FCSTD DOCUMENT  (FreeCAD 0.19R24276 (Git))
Label: Paper_knife
License: All rights reserved
LicenseURL: http://en.wikipedia.org/wiki/All_rights_reserved
objects: Sketcher::SketchObject×2, PartDesign::Body×1
note: 3 computed .brp shape members not serialized (recipe doc carries the construction recipe); baked Part::Feature solids carry a one-line shape summary decoded from their .brp

FEATURE [Sketcher::SketchObject] Sketch  label="Sketch_paper_knife"
  FullyConstrained = false
  MapMode = 5
  Support = -> [XY_Plane]
  sketch-geometry (54):
    g0: Circle CenterX=0 CenterY=0 CenterZ=0 NormalX=0 NormalY=0 NormalZ=1 AngleXU=0 Radius=70
    g1: LineSegment StartX=0 StartY=0 StartZ=0 EndX=-30.5434 EndY=62.9849 EndZ=0
    g2: Circle CenterX=200 CenterY=0 CenterZ=0 NormalX=0 NormalY=0 NormalZ=1 AngleXU=0 Radius=70
    g3: LineSegment StartX=200 StartY=0 StartZ=0 EndX=169.457 EndY=62.9849 EndZ=0
    g4: LineSegment StartX=169.457 StartY=62.9849 StartZ=0 EndX=-30.5434 EndY=62.9849 EndZ=0
    g5: LineSegment StartX=-234.473 StartY=320.288 StartZ=0 EndX=-134.473 EndY=320.288 EndZ=0
    g6: LineSegment StartX=-224.473 StartY=338.288 StartZ=0 EndX=-124.473 EndY=338.288 EndZ=0
    g7: LineSegment StartX=-134.473 StartY=320.288 StartZ=0 EndX=-124.473 EndY=338.288 EndZ=0
    g8: LineSegment StartX=-234.473 StartY=320.288 StartZ=0 EndX=-224.473 EndY=338.288 EndZ=0
    g9: Circle CenterX=-140.473 CenterY=329.288 CenterZ=0 NormalX=0 NormalY=0 NormalZ=1 AngleXU=0 Radius=2.3784
    g10: LineSegment StartX=-233.473 StartY=322.088 StartZ=0 EndX=-133.473 EndY=322.088 EndZ=0
    g11: Circle CenterX=0 CenterY=0 CenterZ=0 NormalX=0 NormalY=0 NormalZ=1 AngleXU=0 Radius=37.5
    g12: Circle CenterX=200 CenterY=0 CenterZ=0 NormalX=0 NormalY=0 NormalZ=1 AngleXU=0 Radius=37.5
    g13: Circle CenterX=169.457 CenterY=62.9849 CenterZ=0 NormalX=0 NormalY=0 NormalZ=1 AngleXU=0 Radius=8
    g14: Circle CenterX=-30.5434 CenterY=62.9849 CenterZ=0 NormalX=0 NormalY=0 NormalZ=1 AngleXU=0 Radius=8
    g15: Circle CenterX=169.457 CenterY=62.9849 CenterZ=0 NormalX=0 NormalY=0 NormalZ=1 AngleXU=0 Radius=2.5
    g16: Circle CenterX=-30.5434 CenterY=62.9849 CenterZ=0 NormalX=0 NormalY=0 NormalZ=1 AngleXU=0 Radius=2.5
    g17: Circle CenterX=70.5033 CenterY=148.864 CenterZ=0 NormalX=0 NormalY=0 NormalZ=1 AngleXU=0 Radius=2.5
    g18: LineSegment StartX=-51.9967 StartY=177.072 StartZ=0 EndX=70.5033 EndY=177.072 EndZ=0
    g19: ArcOfCircle CenterX=75.3046 CenterY=153.864 CenterZ=0 NormalX=0 NormalY=0 NormalZ=1 AngleXU=0 Radius=16 StartAngle=4.17347 EndAngle=5.96536
    g20: LineSegment StartX=75.3046 StartY=153.864 StartZ=0 EndX=75.3046 EndY=137.864 EndZ=0
    g21: ArcOfCircle CenterX=-27.4967 CenterY=156.388 CenterZ=0 NormalX=0 NormalY=0 NormalZ=1 AngleXU=0 Radius=8 StartAngle=3.71141 EndAngle=5.43055
    g22: LineSegment StartX=-59.4967 StartY=163.072 StartZ=0 EndX=-51.9967 EndY=177.072 EndZ=0
    g23: LineSegment StartX=-59.4967 StartY=163.072 StartZ=0 EndX=-55.4967 EndY=152.072 EndZ=0
    g24: ArcOfCircle CenterX=30.0139 CenterY=78.0754 CenterZ=0 NormalX=0 NormalY=0 NormalZ=1 AngleXU=0 Radius=72.29 StartAngle=1.03221 EndAngle=1.56403
    g25: LineSegment StartX=30.5033 StartY=150.364 StartZ=0 EndX=-22.2327 EndY=150.364 EndZ=0
    g26: LineSegment StartX=-34.2327 StartY=152.072 StartZ=0 EndX=-55.4967 EndY=152.072 EndZ=0
    g27: ArcOfCircle CenterX=64.5033 CenterY=151.624 CenterZ=0 NormalX=0 NormalY=0 NormalZ=1 AngleXU=0 Radius=26.1461 StartAngle=6.17743 EndAngle=7.62244
    g28: LineSegment StartX=70.5033 StartY=148.864 StartZ=0 EndX=90.5033 EndY=148.864 EndZ=0
    g29: ArcOfCircle CenterX=-48.4967 CenterY=163.072 CenterZ=0 NormalX=0 NormalY=0 NormalZ=1 AngleXU=0 Radius=2.5 StartAngle=1.5708 EndAngle=4.71239
    g30: ArcOfCircle CenterX=41.5033 CenterY=163.072 CenterZ=0 NormalX=0 NormalY=0 NormalZ=1 AngleXU=0 Radius=2.5 StartAngle=4.71239 EndAngle=7.85398
    g31: LineSegment StartX=-48.4967 StartY=160.572 StartZ=0 EndX=41.5033 EndY=160.572 EndZ=0
    g32: LineSegment StartX=-48.4967 StartY=165.572 StartZ=0 EndX=41.5033 EndY=165.572 EndZ=0
    g33: LineSegment StartX=-27.3628 StartY=293.719 StartZ=0 EndX=-27.3628 EndY=353.575 EndZ=0
    g34: LineSegment StartX=-142.497 StartY=154.072 StartZ=0 EndX=-42.4967 EndY=154.072 EndZ=0
    g35: LineSegment StartX=-132.497 StartY=172.072 StartZ=0 EndX=-32.4967 EndY=172.072 EndZ=0
    g36: LineSegment StartX=-42.4967 StartY=154.072 StartZ=0 EndX=-32.4967 EndY=172.072 EndZ=0
    g37: LineSegment StartX=-142.497 StartY=154.072 StartZ=0 EndX=-132.497 EndY=172.072 EndZ=0
    g38: Circle CenterX=-48.4967 CenterY=163.072 CenterZ=0 NormalX=0 NormalY=0 NormalZ=1 AngleXU=0 Radius=2.3784
    g39: LineSegment StartX=-141.497 StartY=155.872 StartZ=0 EndX=-41.4967 EndY=155.872 EndZ=0
    g40: LineSegment StartX=-69.9968 StartY=0.665106 StartZ=0 EndX=-139.997 EndY=0.665106 EndZ=0
    g41: Circle CenterX=-89.4605 CenterY=142.072 CenterZ=0 NormalX=0 NormalY=0 NormalZ=1 AngleXU=0 Radius=8
    g42: Circle CenterX=60.5395 CenterY=142.072 CenterZ=0 NormalX=0 NormalY=0 NormalZ=1 AngleXU=0 Radius=8
    g43: LineSegment StartX=60.5395 StartY=142.072 StartZ=0 EndX=-89.4605 EndY=142.072 EndZ=0
    g44: LineSegment StartX=-57.421 StartY=157.364 StartZ=0 EndX=70.5033 EndY=157.364 EndZ=0
    g45: LineSegment StartX=-57.7333 StartY=166.364 StartZ=0 EndX=57.5033 EndY=166.364 EndZ=0
    g46: LineSegment StartX=73.0033 StartY=148.864 StartZ=0 EndX=73.0033 EndY=154.864 EndZ=0
    g47: LineSegment StartX=70.5033 StartY=148.864 StartZ=0 EndX=73.0033 EndY=148.864 EndZ=0
    g48: ArcOfCircle CenterX=70.5033 CenterY=154.864 CenterZ=0 NormalX=0 NormalY=0 NormalZ=1 AngleXU=0 Radius=2.5 StartAngle=-9e-16 EndAngle=1.5708
    g49: LineSegment StartX=73.0033 StartY=154.864 StartZ=0 EndX=70.5033 EndY=154.864 EndZ=0
    g50: LineSegment StartX=70.5033 StartY=148.864 StartZ=0 EndX=70.5033 EndY=157.364 EndZ=0
    g51: LineSegment StartX=70.5033 StartY=148.864 StartZ=0 EndX=70.5033 EndY=177.072 EndZ=0
    g52: LineSegment StartX=64.0033 StartY=172.864 StartZ=0 EndX=64.0033 EndY=177.072 EndZ=0
    g53: LineSegment StartX=57.5033 StartY=166.364 StartZ=0 EndX=64.0033 EndY=172.864 EndZ=0
  constraints (141):
    c: Coincident(g0,g-1)
    c: Coincident(g1,g-1)
    c: PointOnObject(g1,g0)
    c: Diameter(g0) = 140
    c: PointOnObject(g2,g-1)
    c: DistanceX(g-1,g2) = 200
    c: Equal(g2,g0)
    c: Coincident(g3,g2)
    c: PointOnObject(g3,g2)
    c: Coincident(g4,g3)
    c: Coincident(g4,g1)
    c: DistanceX(g4,g4) = 200
    c: Horizontal(g5)
    c: Horizontal(g6)
    c: Coincident(g7,g5)
    c: Coincident(g7,g6)
    c: Coincident(g8,g5)
    c: Coincident(g6,g8)
    c: Parallel(g8,g7)
    c: DistanceY(g5,g6) = 18
    c: DistanceX(g5,g5) = 100
    c: DistanceX(g5,g6) = 110
    c: DistanceX(g9,g5) = 6
    c: DistanceY(g5,g9) = 9
    c: PointOnObject(g10,g8)
    c: PointOnObject(g10,g7)
    c: Horizontal(g10)
    c: DistanceY(g5,g10) = 1.8
    c: Coincident(g11,g-1)
    c: Coincident(g12,g2)
    c: Equal(g12,g11)
    c: Diameter(g12) = 75
    c: Coincident(g13,g3)
    c: Diameter(g13) = 16
    c: Coincident(g14,g1)
    c: Equal(g14,g13)
    c: Coincident(g15,g3)
    c: Coincident(g16,g1)
    c: Equal(g16,g15)
    c: Diameter(g15) = 5
    c: Diameter(g17) = 5
    c: Horizontal(g18)
    c: Coincident(g20,g19)
    c: PointOnObject(g20,g19)
    c: Vertical(g20)
    c: DistanceX(g21,g17) = 98
    c: Diameter(g21) = 16
    c: DistanceX(g21,g21) = 12
    c: Coincident(g23,g22)
    c: DistanceX(g23,g17) = 126
    c: DistanceY(g23,g22) = 11
    c: DistanceY(g23,g22) = 25
    c: DistanceX(g24,g17) = 40
    c: Coincident(g19,g24)
    c: Diameter(g24) = 144.58
    c: Coincident(g25,g24)
    c: Coincident(g25,g21)
    c: Horizontal(g25)
    c: Coincident(g26,g21)
    c: Coincident(g26,g23)
    c: Horizontal(g26)
    c: DistanceX(g22,g23) = 4
    c: Coincident(g27,g19)
    c: Coincident(g18,g27)
    c: Coincident(g18,g22)
    c: DistanceX(g22,g18) = 7.5
    c: Coincident(g28,g17)
    c: Horizontal(g28)
    c: DistanceY(g20,g17) = 11
    c: Diameter(g19) = 32
    c: Coincident(g28,g19)
    c: DistanceX(g27,g17) = 6
    c: DistanceY(g17,g27) = 2.76
    c: DistanceX(g17,g19) = 20
    c: Tangent(g29,g32) = 1.5708
    c: Tangent(g29,g31) = -1.5708
    c: Tangent(g31,g30) = -1.5708
    c: Tangent(g32,g30) = 1.5708
    c: Horizontal(g31)
    c: Equal(g29,g30)
    c: Diameter(g30) = 5
    c: Vertical(g33)
    c: Horizontal(g34)
    c: Horizontal(g35)
    c: Coincident(g36,g34)
    c: Coincident(g36,g35)
    c: Coincident(g37,g34)
    c: Coincident(g35,g37)
    c: Parallel(g37,g36)
    c: DistanceY(g34,g35) = 18
    c: Equal(g5,g34) = 100
    c: DistanceX(g34,g35) = 110
    c: DistanceX(g38,g34) = 6
    c: DistanceY(g34,g38) = 9
    c: PointOnObject(g39,g37)
    c: PointOnObject(g39,g36)
    c: Horizontal(g39)
    c: DistanceY(g34,g39) = 1.8
    c: DistanceY(g23,g29) = 11
    c: Coincident(g38,g29)
    c: DistanceX(g23,g29) = 7
    c: DistanceX(g23,g30) = 97
    c: PointOnObject(g40,g0)
    c: Horizontal(g40)
    c: DistanceX(g40,g40) = 70
    c: DistanceX(g19,g17) = 3.41
    c: DistanceY(g17,g24) = 1.5
    c: Coincident(g43,g42)
    c: Coincident(g43,g41)
    c: Horizontal(g43)
    c: Diameter(g42) = 16
    c: Equal(g41,g42)
    c: DistanceX(g43,g43) = 150
    c: DistanceY(g41,g23) = 10
    c: Horizontal(g44)
    c: Horizontal(g45)
    c: DistanceY(g24,g44) = 7
    c: PointOnObject(g44,g23)
    c: PointOnObject(g45,g22)
    c: PointOnObject(g46,g17)
    c: Vertical(g46)
    c: Coincident(g47,g17)
    c: Coincident(g47,g46)
    c: Horizontal(g47)
    c: Diameter(g48) = 5
    c: Coincident(g49,g46)
    c: Horizontal(g49)
    c: Coincident(g48,g46)
    c: Coincident(g48,g44)
    c: Coincident(g49,g48)
    c: Coincident(g50,g17)
    c: Coincident(g50,g48)
    c: Vertical(g50)
    c: DistanceY(g17,g45) = 17.5
    c: Coincident(g51,g17)
    c: Coincident(g51,g18)
    c: Vertical(g51)
    c: PointOnObject(g52,g18)
    c: Coincident(g53,g45)
    c: DistanceX(g52,g17) = 6.5
    c: Angle(g53,g45) = 2.35619
FEATURE [Sketcher::SketchObject] Sketch001  label="Sketch001_master_sketch"
  FullyConstrained = false
  MapMode = 5
  Support = -> [XY_Plane]
  sketch-geometry (11):
    g0: Circle CenterX=0 CenterY=0 CenterZ=0 NormalX=0 NormalY=0 NormalZ=1 AngleXU=0 Radius=70
    g1: LineSegment StartX=0 StartY=0 StartZ=0 EndX=-51.2751 EndY=47.6536 EndZ=0
    g2: Circle CenterX=150 CenterY=0 CenterZ=0 NormalX=0 NormalY=0 NormalZ=1 AngleXU=0 Radius=70
    g3: LineSegment StartX=150 StartY=0 StartZ=0 EndX=98.7249 EndY=47.6536 EndZ=0
    g4: LineSegment StartX=98.7249 StartY=47.6536 StartZ=0 EndX=-51.2751 EndY=47.6536 EndZ=0
    g5: Circle CenterX=0 CenterY=0 CenterZ=0 NormalX=0 NormalY=0 NormalZ=1 AngleXU=0 Radius=44.925
    g6: Circle CenterX=150 CenterY=0 CenterZ=0 NormalX=0 NormalY=0 NormalZ=1 AngleXU=0 Radius=44.925
    g7: Circle CenterX=98.7249 CenterY=47.6536 CenterZ=0 NormalX=0 NormalY=0 NormalZ=1 AngleXU=0 Radius=8
    g8: Circle CenterX=-51.2751 CenterY=47.6536 CenterZ=0 NormalX=0 NormalY=0 NormalZ=1 AngleXU=0 Radius=8
    g9: Circle CenterX=98.7249 CenterY=47.6536 CenterZ=0 NormalX=0 NormalY=0 NormalZ=1 AngleXU=0 Radius=2.5
    g10: Circle CenterX=-51.2751 CenterY=47.6536 CenterZ=0 NormalX=0 NormalY=0 NormalZ=1 AngleXU=0 Radius=2.5
  constraints (24):
    c: Coincident(g0,g-1)
    c: Coincident(g1,g-1)
    c: PointOnObject(g1,g0)
    c: Diameter(g0) = 140
    c: PointOnObject(g2,g-1)
    c: DistanceX(g-1,g2) = 150
    c: Equal(g2,g0)
    c: Coincident(g3,g2)
    c: PointOnObject(g3,g2)
    c: Coincident(g4,g3)
    c: Coincident(g4,g1)
    c: Coincident(g5,g-1)
    c: Coincident(g6,g2)
    c: Equal(g6,g5)
    c: Diameter(g6) = 89.85
    c: Coincident(g7,g3)
    c: Diameter(g7) = 16
    c: Coincident(g8,g1)
    c: Equal(g8,g7)
    c: Coincident(g9,g3)
    c: Coincident(g10,g1)
    c: Equal(g10,g9)
    c: Diameter(g9) = 5
    c: Parallel(g3,g1)
FEATURE [PartDesign::Body] Body
  Group = -> [Sketch,Sketch001]
  Origin = -> Origin
